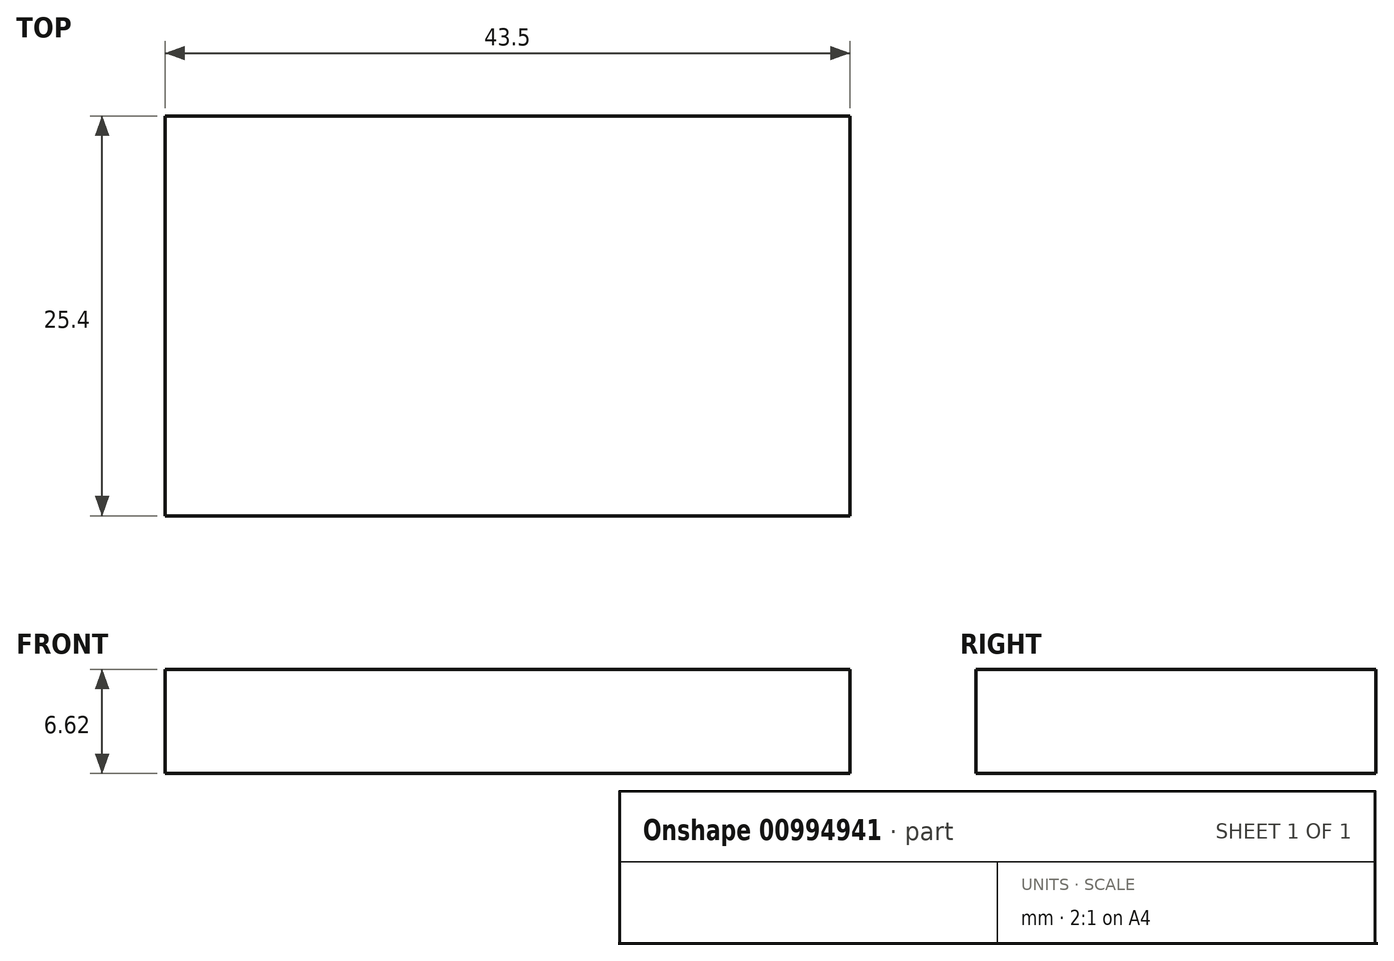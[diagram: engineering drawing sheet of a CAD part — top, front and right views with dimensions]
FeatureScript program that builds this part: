
annotation { "Feature Type Name" : "Feature", "Feature Type Description" : "" }
export const myFeature = defineFeature(function(context is Context, id is Id, definition is map)
    precondition{}
    {
        {
            var Q0;
            Q0=qCreatedBy(makeId("Front.planeOp"),FACE);
            var sketch = newSketch(context, id + "F0", { "sketchPlane" : qUnion([Q0])});
            skPoint(sketch, "E0", {"position": v(0, 46.72) * mm});
            skSolve(sketch);
        }
        {
            var Q0;
            Q0=qCreatedBy(makeId("Front.planeOp"),FACE);
            var sketch = newSketch(context, id + "F1", { "sketchPlane" : qUnion([Q0])});
            skLineSegment(sketch, "E1.bottom", {"start": v(-23.38, 51.73) * mm, "end": v(20.12, 51.73) * mm});
            skLineSegment(sketch, "E1.top", {"start": v(-23.38, 45.11) * mm, "end": v(20.12, 45.11) * mm});
            skLineSegment(sketch, "E1.left", {"start": v(-23.38, 51.73) * mm, "end": v(-23.38, 45.11) * mm});
            skLineSegment(sketch, "E1.right", {"start": v(20.12, 51.73) * mm, "end": v(20.12, 45.11) * mm});
            skSolve(sketch);
        }
        {
            var Q0;
            Q0 = qSketchRegion(id + "F1", true);
            var Q1;
            Q1=makeQuery(id+"F1.imprint","IMPRINT",FACE,{"disambiguationData":[TD([[makeQuery(id+"F1.imprint","IMPRINT",EDGE,{"derivedFrom":sQuery(id+"F1.wireOp",EDGE,"E1.bottom")}),-1.0]])]});
            extrude(context, id + "F2", {"entities" : qUnion([Q0, Q1]), "depth" : 25.4 * mm, "offsetDistance" : 25.4 * mm});
        }
    });
